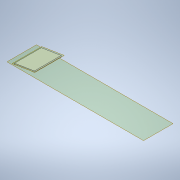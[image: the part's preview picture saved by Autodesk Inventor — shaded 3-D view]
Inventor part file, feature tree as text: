
AUTODESK INVENTOR PART (.ipt)
format: ipt  version: 2020.2 (Build 242310000, 310)  size: 120,832 bytes
history: native  units: mm
features: extrude x3, sketch x3, other x2
ambient origin geometry x8: Origin, YZ Plane, XZ Plane, XY Plane, X Axis, Y Axis, Z Axis, Center Point
bodies: Solide1 (feature_tree)
feature tree (8):
  extrude  "Extrusion1"  Depth=785.7mm
  other  "Plan de construction1"
  extrude  "Extrusion2"  Depth=3.0mm
  other  "Plan de construction2"
  extrude  "Extrusion3"  Depth=14.3mm
  sketch  "Esquisse1"
  sketch  "Esquisse2"
  sketch  "Esquisse3"
